# Revit family: SHH120G-B
name_source: partatom
category: Detail Items
revit_build: Autodesk Revit 2016 (Build: 20150220_1215(x64)
units: mm (PartAtom-declared; Revit-internal decimal feet)

## family parameters
OmniClass Number = 23.20.40.11.24.14
OmniClass Title = Wood Connectors
Rotate with component = No
Shared = No

## types (4) — shared parameters
Density = 1.55 kg
Description = Connector Other
EPD = https://www.strongtie.eu
ETA / DoP = https://www.strongtie.eu
Manufacturer = Simpson Strong-Tie
Model = SHH120
Model Disclaimer = Contact Simpson Strong-Tie Company  for more information
Model ID = 0001207541412101535012325926438910474675
Name = SHH120
ObjectType = SHH120
Product Material = HotDipGalvanised
Product Type = Connector Other
Reference = SHH120G-B
Technical datasheet = https://www.strongtie.eu
URL = www.strongtie.eu
UniClass Number = Pr_20_29_31_44
UniClass Title = Joist hangers

## per-type parameters (varying)
| type | _visiblefront | _visibleleft | _visibleright | _visibletop |
| SST_SHH120_Front | Yes | No | No | No |
| SST_SHH120_Top | No | No | No | Yes |
| SST_SHH120_Left | No | Yes | No | No |
| SST_SHH120_Right | No | No | Yes | No |

## geometry (parser evidence)
native form markers: Sweep x2
no freeform markers — native parametric forms only
